FCSTD DOCUMENT  (FreeCAD 0.18.4R)
Label: Pino
License: All rights reserved
LicenseURL: http://en.wikipedia.org/wiki/All_rights_reserved
objects: Part::Part2DObjectPython×136, Part::Mirroring×9, App::DocumentObjectGroup×1
note: 145 computed .brp shape members not serialized (recipe doc carries the construction recipe); baked Part::Feature solids carry a one-line shape summary decoded from their .brp

FEATURE [Part::Part2DObjectPython] Line001  # Draft 2D object (typed FeaturePython)
  ChamferSize = 0
  Closed = false
  End = (5.7,0,0)
  FilletRadius = 0
  Length = 11.4
  MakeFace = true
  Points = (2) [(-5.7,0,0),(5.7,0,0)]
  Start = (-5.7,0,0)
  Subdivisions = 0
FEATURE [Part::Part2DObjectPython] Line003  # Draft 2D object (typed FeaturePython)
  ChamferSize = 0
  Closed = false
  End = (-5.7,0,0)
  FilletRadius = 0
  Length = 91.1954
  MakeFace = true
  Placement = pos=(-5.7,0,0) rot=(0,0,1;0rad)
  Points = (2) [(-88.088,23.6031,0),(-2.66454e-15,0,0)]
  Start = (-93.788,23.6031,0)
  Subdivisions = 0
FEATURE [Part::Part2DObjectPython] Line004  # Draft 2D object (typed FeaturePython)
  ChamferSize = 0
  Closed = true
  End = (89.7247,38.7673,0)
  FilletRadius = 0
  Length = 5.7
  MakeFace = false
  Placement = pos=(91.2,33.2615,0) rot=(0,0,1;0rad)
  Points = (2) [(0,0,0),(-1.47527,5.50578,0)]
  Start = (91.2,33.2615,0)
  Subdivisions = 0
FEATURE [Part::Part2DObjectPython] Line005  # Draft 2D object (typed FeaturePython)
  ChamferSize = 0
  Closed = false
  End = (-89.7247,38.7673,0)
  FilletRadius = 0
  Length = 5.7
  MakeFace = true
  Placement = pos=(-91.2,33.2615,0) rot=(0,0,1;0rad)
  Points = (2) [(0,0,0),(1.47527,5.50578,0)]
  Start = (-91.2,33.2615,0)
  Subdivisions = 0
FEATURE [Part::Part2DObjectPython] Line007  # Draft 2D object (typed FeaturePython)
  ChamferSize = 0
  Closed = false
  End = (-91.2,33.2615,0)
  FilletRadius = 0
  Length = 9.99914
  MakeFace = true
  Placement = pos=(-91.2,33.2615,0) rot=(0,0,1;0rad)
  Points = (2) [(-2.58797,-9.65843,0),(0,0,0)]
  Start = (-93.788,23.6031,0)
  Subdivisions = 0
FEATURE [Part::Part2DObjectPython] Line011  # Draft 2D object (typed FeaturePython)
  ChamferSize = 0
  Closed = true
  End = (78.3247,47.5148,0)
  FilletRadius = 0
  Length = 5.7
  MakeFace = false
  Placement = pos=(79.8,42.0091,0) rot=(0,0,1;0rad)
  Points = (2) [(0,0,0),(-1.47527,5.50578,0)]
  Start = (79.8,42.0091,0)
  Subdivisions = 0
FEATURE [Part::Part2DObjectPython] Line012  # Draft 2D object (typed FeaturePython)
  ChamferSize = 0
  Closed = false
  End = (-78.3247,47.5148,0)
  FilletRadius = 0
  Length = 5.7
  MakeFace = true
  Placement = pos=(-79.8,42.0091,0) rot=(0,0,1;0rad)
  Points = (2) [(0,0,0),(1.47527,5.50578,0)]
  Start = (-79.8,42.0091,0)
  Subdivisions = 0
FEATURE [Part::Part2DObjectPython] Line013  # Draft 2D object (typed FeaturePython)
  ChamferSize = 0
  Closed = false
  End = (81.2753,36.5033,0)
  FilletRadius = 0
  Length = 5.7
  MakeFace = true
  Placement = pos=(79.8,42.0091,0) rot=(0,0,1;0rad)
  Points = (2) [(0,0,0),(1.47527,-5.50578,0)]
  Start = (79.8,42.0091,0)
  Subdivisions = 0
FEATURE [Part::Part2DObjectPython] Line014  # Draft 2D object (typed FeaturePython)
  ChamferSize = 0
  Closed = false
  End = (-81.2753,36.5033,0)
  FilletRadius = 0
  Length = 5.7
  MakeFace = true
  Placement = pos=(-79.8,42.0091,0) rot=(0,0,1;0rad)
  Points = (2) [(0,0,0),(-1.47527,-5.50578,0)]
  Start = (-79.8,42.0091,0)
  Subdivisions = 0
FEATURE [Part::Part2DObjectPython] Line018  # Draft 2D object (typed FeaturePython)
  ChamferSize = 0
  Closed = true
  End = (66.9247,56.2624,0)
  FilletRadius = 0
  Length = 5.7
  MakeFace = false
  Placement = pos=(68.4,50.7566,0) rot=(0,0,1;0rad)
  Points = (2) [(0,0,0),(-1.47527,5.50578,0)]
  Start = (68.4,50.7566,0)
  Subdivisions = 0
FEATURE [Part::Part2DObjectPython] Line019  # Draft 2D object (typed FeaturePython)
  ChamferSize = 0
  Closed = false
  End = (-66.9247,56.2624,0)
  FilletRadius = 0
  Length = 5.7
  MakeFace = true
  Placement = pos=(-68.4,50.7566,0) rot=(0,0,1;0rad)
  Points = (2) [(0,0,0),(1.47527,5.50578,0)]
  Start = (-68.4,50.7566,0)
  Subdivisions = 0
FEATURE [Part::Part2DObjectPython] Line020  # Draft 2D object (typed FeaturePython)
  ChamferSize = 0
  Closed = false
  End = (69.8753,45.2508,0)
  FilletRadius = 0
  Length = 5.7
  MakeFace = true
  Placement = pos=(68.4,50.7566,0) rot=(0,0,1;0rad)
  Points = (2) [(0,0,0),(1.47527,-5.50578,0)]
  Start = (68.4,50.7566,0)
  Subdivisions = 0
FEATURE [Part::Part2DObjectPython] Line021  # Draft 2D object (typed FeaturePython)
  ChamferSize = 0
  Closed = false
  End = (-69.8753,45.2508,0)
  FilletRadius = 0
  Length = 5.7
  MakeFace = true
  Placement = pos=(-68.4,50.7566,0) rot=(0,0,1;0rad)
  Points = (2) [(0,0,0),(-1.47527,-5.50578,0)]
  Start = (-68.4,50.7566,0)
  Subdivisions = 0
FEATURE [Part::Part2DObjectPython] Line025  # Draft 2D object (typed FeaturePython)
  ChamferSize = 0
  Closed = true
  End = (55.5247,65.0099,0)
  FilletRadius = 0
  Length = 5.7
  MakeFace = false
  Placement = pos=(57,59.5041,0) rot=(0,0,1;0rad)
  Points = (2) [(0,0,0),(-1.47527,5.50578,0)]
  Start = (57,59.5041,0)
  Subdivisions = 0
FEATURE [Part::Part2DObjectPython] Line026  # Draft 2D object (typed FeaturePython)
  ChamferSize = 0
  Closed = false
  End = (-55.5247,65.0099,0)
  FilletRadius = 0
  Length = 5.7
  MakeFace = true
  Placement = pos=(-57,59.5041,0) rot=(0,0,1;0rad)
  Points = (2) [(0,0,0),(1.47527,5.50578,0)]
  Start = (-57,59.5041,0)
  Subdivisions = 0
FEATURE [Part::Part2DObjectPython] Line027  # Draft 2D object (typed FeaturePython)
  ChamferSize = 0
  Closed = false
  End = (58.4753,53.9983,0)
  FilletRadius = 0
  Length = 5.7
  MakeFace = true
  Placement = pos=(57,59.5041,0) rot=(0,0,1;0rad)
  Points = (2) [(0,0,0),(1.47527,-5.50578,0)]
  Start = (57,59.5041,0)
  Subdivisions = 0
FEATURE [Part::Part2DObjectPython] Line028  # Draft 2D object (typed FeaturePython)
  ChamferSize = 0
  Closed = false
  End = (-58.4753,53.9983,0)
  FilletRadius = 0
  Length = 5.7
  MakeFace = true
  Placement = pos=(-57,59.5041,0) rot=(0,0,1;0rad)
  Points = (2) [(0,0,0),(-1.47527,-5.50578,0)]
  Start = (-57,59.5041,0)
  Subdivisions = 0
FEATURE [Part::Part2DObjectPython] Line032  # Draft 2D object (typed FeaturePython)
  ChamferSize = 0
  Closed = true
  End = (44.1247,73.7574,0)
  FilletRadius = 0
  Length = 5.7
  MakeFace = false
  Placement = pos=(45.6,68.2516,0) rot=(0,0,1;0rad)
  Points = (2) [(0,0,0),(-1.47527,5.50578,0)]
  Start = (45.6,68.2516,0)
  Subdivisions = 0
FEATURE [Part::Part2DObjectPython] Line033  # Draft 2D object (typed FeaturePython)
  ChamferSize = 0
  Closed = false
  End = (-44.1247,73.7574,0)
  FilletRadius = 0
  Length = 5.7
  MakeFace = true
  Placement = pos=(-45.6,68.2516,0) rot=(0,0,1;0rad)
  Points = (2) [(0,0,0),(1.47527,5.50578,0)]
  Start = (-45.6,68.2516,0)
  Subdivisions = 0
FEATURE [Part::Part2DObjectPython] Line034  # Draft 2D object (typed FeaturePython)
  ChamferSize = 0
  Closed = false
  End = (47.0753,62.7459,0)
  FilletRadius = 0
  Length = 5.7
  MakeFace = true
  Placement = pos=(45.6,68.2516,0) rot=(0,0,1;0rad)
  Points = (2) [(0,0,0),(1.47527,-5.50578,0)]
  Start = (45.6,68.2516,0)
  Subdivisions = 0
FEATURE [Part::Part2DObjectPython] Line035  # Draft 2D object (typed FeaturePython)
  ChamferSize = 0
  Closed = false
  End = (-47.0753,62.7459,0)
  FilletRadius = 0
  Length = 5.7
  MakeFace = true
  Placement = pos=(-45.6,68.2516,0) rot=(0,0,1;0rad)
  Points = (2) [(0,0,0),(-1.47527,-5.50578,0)]
  Start = (-45.6,68.2516,0)
  Subdivisions = 0
FEATURE [Part::Part2DObjectPython] Line039  # Draft 2D object (typed FeaturePython)
  ChamferSize = 0
  Closed = true
  End = (32.7247,82.5049,0)
  FilletRadius = 0
  Length = 5.7
  MakeFace = false
  Placement = pos=(34.2,76.9992,0) rot=(0,0,1;0rad)
  Points = (2) [(0,0,0),(-1.47527,5.50578,0)]
  Start = (34.2,76.9992,0)
  Subdivisions = 0
FEATURE [Part::Part2DObjectPython] Line040  # Draft 2D object (typed FeaturePython)
  ChamferSize = 0
  Closed = false
  End = (-32.7247,82.5049,0)
  FilletRadius = 0
  Length = 5.7
  MakeFace = true
  Placement = pos=(-34.2,76.9992,0) rot=(0,0,1;0rad)
  Points = (2) [(0,0,0),(1.47527,5.50578,0)]
  Start = (-34.2,76.9992,0)
  Subdivisions = 0
FEATURE [Part::Part2DObjectPython] Line041  # Draft 2D object (typed FeaturePython)
  ChamferSize = 0
  Closed = false
  End = (35.6753,71.4934,0)
  FilletRadius = 0
  Length = 5.7
  MakeFace = true
  Placement = pos=(34.2,76.9992,0) rot=(0,0,1;0rad)
  Points = (2) [(0,0,0),(1.47527,-5.50578,0)]
  Start = (34.2,76.9992,0)
  Subdivisions = 0
FEATURE [Part::Part2DObjectPython] Line042  # Draft 2D object (typed FeaturePython)
  ChamferSize = 0
  Closed = false
  End = (-35.6753,71.4934,0)
  FilletRadius = 0
  Length = 5.7
  MakeFace = true
  Placement = pos=(-34.2,76.9992,0) rot=(0,0,1;0rad)
  Points = (2) [(0,0,0),(-1.47527,-5.50578,0)]
  Start = (-34.2,76.9992,0)
  Subdivisions = 0
FEATURE [Part::Part2DObjectPython] Line046  # Draft 2D object (typed FeaturePython)
  ChamferSize = 0
  Closed = true
  End = (21.3247,91.2525,0)
  FilletRadius = 0
  Length = 5.7
  MakeFace = false
  Placement = pos=(22.8,85.7467,0) rot=(0,0,1;0rad)
  Points = (2) [(0,0,0),(-1.47527,5.50578,0)]
  Start = (22.8,85.7467,0)
  Subdivisions = 0
FEATURE [Part::Part2DObjectPython] Line047  # Draft 2D object (typed FeaturePython)
  ChamferSize = 0
  Closed = false
  End = (-21.3247,91.2525,0)
  FilletRadius = 0
  Length = 5.7
  MakeFace = true
  Placement = pos=(-22.8,85.7467,0) rot=(0,0,1;0rad)
  Points = (2) [(0,0,0),(1.47527,5.50578,0)]
  Start = (-22.8,85.7467,0)
  Subdivisions = 0
FEATURE [Part::Part2DObjectPython] Line048  # Draft 2D object (typed FeaturePython)
  ChamferSize = 0
  Closed = false
  End = (24.2753,80.2409,0)
  FilletRadius = 0
  Length = 5.7
  MakeFace = true
  Placement = pos=(22.8,85.7467,0) rot=(0,0,1;0rad)
  Points = (2) [(0,0,0),(1.47527,-5.50578,0)]
  Start = (22.8,85.7467,0)
  Subdivisions = 0
FEATURE [Part::Part2DObjectPython] Line049  # Draft 2D object (typed FeaturePython)
  ChamferSize = 0
  Closed = false
  End = (-24.2753,80.2409,0)
  FilletRadius = 0
  Length = 5.7
  MakeFace = true
  Placement = pos=(-22.8,85.7467,0) rot=(0,0,1;0rad)
  Points = (2) [(0,0,0),(-1.47527,-5.50578,0)]
  Start = (-22.8,85.7467,0)
  Subdivisions = 0
FEATURE [Part::Part2DObjectPython] Line053  # Draft 2D object (typed FeaturePython)
  ChamferSize = 0
  Closed = true
  End = (9.92473,100,0)
  FilletRadius = 0
  Length = 5.7
  MakeFace = false
  Placement = pos=(11.4,94.4942,0) rot=(0,0,1;0rad)
  Points = (2) [(0,0,0),(-1.47527,5.50578,0)]
  Start = (11.4,94.4942,0)
  Subdivisions = 0
FEATURE [Part::Part2DObjectPython] Line054  # Draft 2D object (typed FeaturePython)
  ChamferSize = 0
  Closed = false
  End = (-9.92473,100,0)
  FilletRadius = 0
  Length = 5.7
  MakeFace = true
  Placement = pos=(-11.4,94.4942,0) rot=(0,0,1;0rad)
  Points = (2) [(0,0,0),(1.47527,5.50578,0)]
  Start = (-11.4,94.4942,0)
  Subdivisions = 0
FEATURE [Part::Part2DObjectPython] Line055  # Draft 2D object (typed FeaturePython)
  ChamferSize = 0
  Closed = false
  End = (12.8753,88.9884,0)
  FilletRadius = 0
  Length = 5.7
  MakeFace = true
  Placement = pos=(11.4,94.4942,0) rot=(0,0,1;0rad)
  Points = (2) [(0,0,0),(1.47527,-5.50578,0)]
  Start = (11.4,94.4942,0)
  Subdivisions = 0
FEATURE [Part::Part2DObjectPython] Line056  # Draft 2D object (typed FeaturePython)
  ChamferSize = 0
  Closed = false
  End = (-12.8753,88.9884,0)
  FilletRadius = 0
  Length = 5.7
  MakeFace = true
  Placement = pos=(-11.4,94.4942,0) rot=(0,0,1;0rad)
  Points = (2) [(0,0,0),(-1.47527,-5.50578,0)]
  Start = (-11.4,94.4942,0)
  Subdivisions = 0
FEATURE [Part::Part2DObjectPython] Line057  # Draft 2D object (typed FeaturePython)
  ChamferSize = 0
  Closed = false
  End = (-81.2753,36.5033,0)
  FilletRadius = 0
  Length = 8.74753
  MakeFace = true
  Placement = pos=(-89.7247,38.7673,0) rot=(0,0,1;0rad)
  Points = (2) [(0,0,0),(8.44946,-2.26403,0)]
  Start = (-89.7247,38.7673,0)
  Subdivisions = 0
FEATURE [Part::Part2DObjectPython] Line058  # Draft 2D object (typed FeaturePython)
  ChamferSize = 0
  Closed = false
  End = (-69.8753,45.2508,0)
  FilletRadius = 0
  Length = 8.74753
  MakeFace = true
  Placement = pos=(-78.3247,47.5148,0) rot=(0,0,1;0rad)
  Points = (2) [(0,0,0),(8.44946,-2.26403,0)]
  Start = (-78.3247,47.5148,0)
  Subdivisions = 0
FEATURE [Part::Part2DObjectPython] Line059  # Draft 2D object (typed FeaturePython)
  ChamferSize = 0
  Closed = false
  End = (-58.4753,53.9983,0)
  FilletRadius = 0
  Length = 8.74753
  MakeFace = true
  Placement = pos=(-66.9247,56.2624,0) rot=(0,0,1;0rad)
  Points = (2) [(0,0,0),(8.44946,-2.26403,0)]
  Start = (-66.9247,56.2624,0)
  Subdivisions = 0
FEATURE [Part::Part2DObjectPython] Line060  # Draft 2D object (typed FeaturePython)
  ChamferSize = 0
  Closed = false
  End = (-47.0753,62.7459,0)
  FilletRadius = 0
  Length = 8.74753
  MakeFace = true
  Placement = pos=(-55.5247,65.0099,0) rot=(0,0,1;0rad)
  Points = (2) [(0,0,0),(8.44946,-2.26403,0)]
  Start = (-55.5247,65.0099,0)
  Subdivisions = 0
FEATURE [Part::Part2DObjectPython] Line061  # Draft 2D object (typed FeaturePython)
  ChamferSize = 0
  Closed = false
  End = (-35.6753,71.4934,0)
  FilletRadius = 0
  Length = 8.74753
  MakeFace = true
  Placement = pos=(-44.1247,73.7574,0) rot=(0,0,1;0rad)
  Points = (2) [(0,0,0),(8.44946,-2.26403,0)]
  Start = (-44.1247,73.7574,0)
  Subdivisions = 0
FEATURE [Part::Part2DObjectPython] Line062  # Draft 2D object (typed FeaturePython)
  ChamferSize = 0
  Closed = false
  End = (-24.2753,80.2409,0)
  FilletRadius = 0
  Length = 8.74753
  MakeFace = true
  Placement = pos=(-32.7247,82.5049,0) rot=(0,0,1;0rad)
  Points = (2) [(0,0,0),(8.44946,-2.26403,0)]
  Start = (-32.7247,82.5049,0)
  Subdivisions = 0
FEATURE [Part::Part2DObjectPython] Line063  # Draft 2D object (typed FeaturePython)
  ChamferSize = 0
  Closed = false
  End = (-12.8753,88.9884,0)
  FilletRadius = 0
  Length = 8.74753
  MakeFace = true
  Placement = pos=(-21.3247,91.2525,0) rot=(0,0,1;0rad)
  Points = (2) [(0,0,0),(8.44946,-2.26403,0)]
  Start = (-21.3247,91.2525,0)
  Subdivisions = 0
FEATURE [Part::Mirroring] mirror  label="Mirror of Line003"
  Base = (0,91.4396,0)
  Normal = (-1,0,0)
  Source = -> Line003
FEATURE [Part::Mirroring] mirror001  label="Mirror of Line007"
  Base = (0,91.4396,0)
  Normal = (-1,0,0)
  Source = -> Line007
FEATURE [Part::Mirroring] mirror002  label="Mirror of Line057"
  Base = (0,91.4396,0)
  Normal = (-1,0,0)
  Source = -> Line057
FEATURE [Part::Mirroring] mirror003  label="Mirror of Line058"
  Base = (0,91.4396,0)
  Normal = (-1,0,0)
  Source = -> Line058
FEATURE [Part::Mirroring] mirror004  label="Mirror of Line059"
  Base = (0,91.4396,0)
  Normal = (-1,0,0)
  Source = -> Line059
FEATURE [Part::Mirroring] mirror005  label="Mirror of Line060"
  Base = (0,91.4396,0)
  Normal = (-1,0,0)
  Source = -> Line060
FEATURE [Part::Mirroring] mirror006  label="Mirror of Line061"
  Base = (0,91.4396,0)
  Normal = (-1,0,0)
  Source = -> Line061
FEATURE [Part::Mirroring] mirror007  label="Mirror of Line062"
  Base = (0,91.4396,0)
  Normal = (-1,0,0)
  Source = -> Line062
FEATURE [Part::Mirroring] mirror008  label="Mirror of Line063"
  Base = (0,91.4396,0)
  Normal = (-1,0,0)
  Source = -> Line063
FEATURE [Part::Part2DObjectPython] Line065  # Draft 2D object (typed FeaturePython)
  ChamferSize = 0
  Closed = false
  End = (9.92473,100,0)
  FilletRadius = 0
  Length = 19.8495
  MakeFace = true
  Placement = pos=(-9.92473,100,0) rot=(0,0,1;0rad)
  Points = (2) [(0,0,0),(19.8495,0,0)]
  Start = (-9.92473,100,0)
  Subdivisions = 0
FEATURE [App::DocumentObjectGroup] Group  label="Borders"
  Group = -> [Line003,Line007,Line005,Line057,Line014,Line012,Line058,Line021,Line019,Line028,Line026,Line059,Line060,Line035,Line033,Line061,Line042,Line040,Line062,Line049,Line047,Line063,Line056,Line054,Line065,Line053,Line055,mirror008,Line046,Line048,mirror007,Line039,Line041,mirror006,Line032,Line034,mirror005,Line025,Line027,mirror004,Line018,Line020,mirror003,Line011,Line013,mirror002,Line004,Line001,+2 more]
FEATURE [Part::Part2DObjectPython] Line  # Draft 2D object (typed FeaturePython)
  ChamferSize = 0
  Closed = false
  End = (0,8.82456,0)
  FilletRadius = 0
  Length = 8.82456
  MakeFace = true
  Points = (2) [(0,0,0),(0,8.82456,0)]
  Start = (0,0,0)
  Subdivisions = 0
FEATURE [Part::Part2DObjectPython] Line066  # Draft 2D object (typed FeaturePython)
  ChamferSize = 0
  Closed = false
  End = (5.7,0,0)
  FilletRadius = 0
  Length = 11.4
  MakeFace = true
  Points = (2) [(-5.7,0,0),(5.7,0,0)]
  Start = (-5.7,0,0)
  Subdivisions = 0
FEATURE [Part::Part2DObjectPython] Wire  # Draft 2D object (typed FeaturePython)
  ChamferSize = 0
  Closed = true
  End = (0.95,7.00161,0)
  FilletRadius = 0
  Length = 11.2
  MakeFace = false
  Placement = pos=(-0.95,7.00161,0) rot=(0,0,1;0rad)
  Points = (4) [(0,0,0),(0,3.7,0),(1.9,3.7,0),(1.9,0,0)]
  Start = (-0.95,7.00161,0)
  Subdivisions = 0
FEATURE [Part::Part2DObjectPython] Line067  # Draft 2D object (typed FeaturePython)
  ChamferSize = 0
  Closed = false
  End = (91.2,33.2615,0)
  FilletRadius = 0
  Length = 94.4172
  MakeFace = true
  Placement = pos=(0,8.82456,0) rot=(0,0,1;0rad)
  Points = (2) [(0,0,0),(91.2,24.437,0)]
  Start = (0,8.82456,0)
  Subdivisions = 0
FEATURE [Part::Part2DObjectPython] Line068  # Draft 2D object (typed FeaturePython)
  ChamferSize = 0
  Closed = false
  End = (-91.2,33.2615,0)
  FilletRadius = 0
  Length = 94.4172
  MakeFace = true
  Placement = pos=(0,8.82456,0) rot=(0,0,1;0rad)
  Points = (2) [(0,0,0),(-91.2,24.437,0)]
  Start = (0,8.82456,0)
  Subdivisions = 0
FEATURE [Part::Part2DObjectPython] Wire001  # Draft 2D object (typed FeaturePython)
  ChamferSize = 0
  Closed = true
  End = (84.1911,32.367,0)
  FilletRadius = 0
  Length = 11.2
  MakeFace = false
  Placement = pos=(80.6172,31.4094,0) rot=(0,0,1;0rad)
  Points = (4) [(0,0,0),(0.491756,-1.83526,0),(4.06568,-0.877629,0),(3.57393,0.95763,0)]
  Start = (80.6172,31.4094,0)
  Subdivisions = 0
FEATURE [Part::Part2DObjectPython] Wire002  # Draft 2D object (typed FeaturePython)
  ChamferSize = 0
  Closed = true
  End = (-84.1911,32.367,0)
  FilletRadius = 0
  Length = 11.2
  MakeFace = false
  Placement = pos=(-80.6172,31.4094,0) rot=(0,0,1;0rad)
  Points = (4) [(0,0,0),(-0.491756,-1.83526,0),(-4.06568,-0.877629,0),(-3.57393,0.95763,0)]
  Start = (-80.6172,31.4094,0)
  Subdivisions = 0
FEATURE [Part::Part2DObjectPython] Line069  # Draft 2D object (typed FeaturePython)
  ChamferSize = 0
  Closed = true
  End = (89.7247,38.7673,0)
  FilletRadius = 0
  Length = 5.7
  MakeFace = false
  Placement = pos=(91.2,33.2615,0) rot=(0,0,1;0rad)
  Points = (2) [(0,0,0),(-1.47527,5.50578,0)]
  Start = (91.2,33.2615,0)
  Subdivisions = 0
FEATURE [Part::Part2DObjectPython] Line070  # Draft 2D object (typed FeaturePython)
  ChamferSize = 0
  Closed = false
  End = (-89.7247,38.7673,0)
  FilletRadius = 0
  Length = 5.7
  MakeFace = true
  Placement = pos=(-91.2,33.2615,0) rot=(0,0,1;0rad)
  Points = (2) [(0,0,0),(1.47527,5.50578,0)]
  Start = (-91.2,33.2615,0)
  Subdivisions = 0
FEATURE [Part::Part2DObjectPython] Line071  # Draft 2D object (typed FeaturePython)
  ChamferSize = 0
  Closed = false
  End = (92.6753,27.7558,0)
  FilletRadius = 0
  Length = 5.7
  MakeFace = true
  Placement = pos=(91.2,33.2615,0) rot=(0,0,1;0rad)
  Points = (2) [(0,0,0),(1.47527,-5.50578,0)]
  Start = (91.2,33.2615,0)
  Subdivisions = 0
FEATURE [Part::Part2DObjectPython] Line072  # Draft 2D object (typed FeaturePython)
  ChamferSize = 0
  Closed = false
  End = (-92.6753,27.7558,0)
  FilletRadius = 0
  Length = 5.7
  MakeFace = true
  Placement = pos=(-91.2,33.2615,0) rot=(0,0,1;0rad)
  Points = (2) [(0,0,0),(-1.47527,-5.50578,0)]
  Start = (-91.2,33.2615,0)
  Subdivisions = 0
FEATURE [Part::Part2DObjectPython] Circle  # Draft 2D object (typed FeaturePython)
  FirstAngle = 0
  LastAngle = 0
  MakeFace = false
  Placement = pos=(47.0753,15.5373,0) rot=(0,0,1;0rad)
  Radius = 0.45
FEATURE [Part::Part2DObjectPython] Circle001  # Draft 2D object (typed FeaturePython)
  FirstAngle = 0
  LastAngle = 0
  MakeFace = false
  Placement = pos=(-47.0753,15.5373,0) rot=(0,0,1;0rad)
  Radius = 0.45
FEATURE [Part::Part2DObjectPython] Line073  # Draft 2D object (typed FeaturePython)
  ChamferSize = 0
  Closed = false
  End = (0,20.6267,0)
  FilletRadius = 0
  Length = 11.8021
  MakeFace = true
  Placement = pos=(0,8.82456,0) rot=(0,0,1;0rad)
  Points = (2) [(0,0,0),(0,11.8021,0)]
  Start = (0,8.82456,0)
  Subdivisions = 0
FEATURE [Part::Part2DObjectPython] Line074  # Draft 2D object (typed FeaturePython)
  ChamferSize = 0
  Closed = false
  End = (79.8,42.0091,0)
  FilletRadius = 0
  Length = 82.615
  MakeFace = true
  Placement = pos=(0,20.6267,0) rot=(0,0,1;0rad)
  Points = (2) [(0,0,0),(79.8,21.3823,0)]
  Start = (0,20.6267,0)
  Subdivisions = 0
FEATURE [Part::Part2DObjectPython] Line075  # Draft 2D object (typed FeaturePython)
  ChamferSize = 0
  Closed = false
  End = (-79.8,42.0091,0)
  FilletRadius = 0
  Length = 82.615
  MakeFace = true
  Placement = pos=(0,20.6267,0) rot=(0,0,1;0rad)
  Points = (2) [(0,0,0),(-79.8,21.3823,0)]
  Start = (0,20.6267,0)
  Subdivisions = 0
FEATURE [Part::Part2DObjectPython] Wire003  # Draft 2D object (typed FeaturePython)
  ChamferSize = 0
  Closed = true
  End = (72.7911,41.1145,0)
  FilletRadius = 0
  Length = 11.2
  MakeFace = false
  Placement = pos=(69.2172,40.1569,0) rot=(0,0,1;0rad)
  Points = (4) [(0,0,0),(0.491756,-1.83526,0),(4.06568,-0.877629,0),(3.57393,0.95763,0)]
  Start = (69.2172,40.1569,0)
  Subdivisions = 0
FEATURE [Part::Part2DObjectPython] Wire004  # Draft 2D object (typed FeaturePython)
  ChamferSize = 0
  Closed = true
  End = (-72.7911,41.1145,0)
  FilletRadius = 0
  Length = 11.2
  MakeFace = false
  Placement = pos=(-69.2172,40.1569,0) rot=(0,0,1;0rad)
  Points = (4) [(0,0,0),(-0.491756,-1.83526,0),(-4.06568,-0.877629,0),(-3.57393,0.95763,0)]
  Start = (-69.2172,40.1569,0)
  Subdivisions = 0
FEATURE [Part::Part2DObjectPython] Line076  # Draft 2D object (typed FeaturePython)
  ChamferSize = 0
  Closed = true
  End = (78.3247,47.5148,0)
  FilletRadius = 0
  Length = 5.7
  MakeFace = false
  Placement = pos=(79.8,42.0091,0) rot=(0,0,1;0rad)
  Points = (2) [(0,0,0),(-1.47527,5.50578,0)]
  Start = (79.8,42.0091,0)
  Subdivisions = 0
FEATURE [Part::Part2DObjectPython] Line077  # Draft 2D object (typed FeaturePython)
  ChamferSize = 0
  Closed = false
  End = (-78.3247,47.5148,0)
  FilletRadius = 0
  Length = 5.7
  MakeFace = true
  Placement = pos=(-79.8,42.0091,0) rot=(0,0,1;0rad)
  Points = (2) [(0,0,0),(1.47527,5.50578,0)]
  Start = (-79.8,42.0091,0)
  Subdivisions = 0
FEATURE [Part::Part2DObjectPython] Line078  # Draft 2D object (typed FeaturePython)
  ChamferSize = 0
  Closed = false
  End = (81.2753,36.5033,0)
  FilletRadius = 0
  Length = 5.7
  MakeFace = true
  Placement = pos=(79.8,42.0091,0) rot=(0,0,1;0rad)
  Points = (2) [(0,0,0),(1.47527,-5.50578,0)]
  Start = (79.8,42.0091,0)
  Subdivisions = 0
FEATURE [Part::Part2DObjectPython] Line079  # Draft 2D object (typed FeaturePython)
  ChamferSize = 0
  Closed = false
  End = (-81.2753,36.5033,0)
  FilletRadius = 0
  Length = 5.7
  MakeFace = true
  Placement = pos=(-79.8,42.0091,0) rot=(0,0,1;0rad)
  Points = (2) [(0,0,0),(-1.47527,-5.50578,0)]
  Start = (-79.8,42.0091,0)
  Subdivisions = 0
FEATURE [Part::Part2DObjectPython] Circle002  # Draft 2D object (typed FeaturePython)
  FirstAngle = 0
  LastAngle = 0
  MakeFace = false
  Placement = pos=(41.3753,25.8121,0) rot=(0,0,1;0rad)
  Radius = 0.45
FEATURE [Part::Part2DObjectPython] Circle003  # Draft 2D object (typed FeaturePython)
  FirstAngle = 0
  LastAngle = 0
  MakeFace = false
  Placement = pos=(-41.3753,25.8121,0) rot=(0,0,1;0rad)
  Radius = 0.45
FEATURE [Part::Part2DObjectPython] Line080  # Draft 2D object (typed FeaturePython)
  ChamferSize = 0
  Closed = false
  End = (0,32.4289,0)
  FilletRadius = 0
  Length = 11.8021
  MakeFace = true
  Placement = pos=(0,20.6267,0) rot=(0,0,1;0rad)
  Points = (2) [(0,0,0),(0,11.8021,0)]
  Start = (0,20.6267,0)
  Subdivisions = 0
FEATURE [Part::Part2DObjectPython] Line081  # Draft 2D object (typed FeaturePython)
  ChamferSize = 0
  Closed = false
  End = (68.4,50.7566,0)
  FilletRadius = 0
  Length = 70.8129
  MakeFace = true
  Placement = pos=(0,32.4289,0) rot=(0,0,1;0rad)
  Points = (2) [(0,0,0),(68.4,18.3277,0)]
  Start = (0,32.4289,0)
  Subdivisions = 0
FEATURE [Part::Part2DObjectPython] Line082  # Draft 2D object (typed FeaturePython)
  ChamferSize = 0
  Closed = false
  End = (-68.4,50.7566,0)
  FilletRadius = 0
  Length = 70.8129
  MakeFace = true
  Placement = pos=(0,32.4289,0) rot=(0,0,1;0rad)
  Points = (2) [(0,0,0),(-68.4,18.3277,0)]
  Start = (0,32.4289,0)
  Subdivisions = 0
FEATURE [Part::Part2DObjectPython] Wire005  # Draft 2D object (typed FeaturePython)
  ChamferSize = 0
  Closed = true
  End = (61.3911,49.8621,0)
  FilletRadius = 0
  Length = 11.2
  MakeFace = false
  Placement = pos=(57.8172,48.9044,0) rot=(0,0,1;0rad)
  Points = (4) [(0,0,0),(0.491756,-1.83526,0),(4.06568,-0.877629,0),(3.57393,0.95763,0)]
  Start = (57.8172,48.9044,0)
  Subdivisions = 0
FEATURE [Part::Part2DObjectPython] Wire006  # Draft 2D object (typed FeaturePython)
  ChamferSize = 0
  Closed = true
  End = (-61.3911,49.8621,0)
  FilletRadius = 0
  Length = 11.2
  MakeFace = false
  Placement = pos=(-57.8172,48.9044,0) rot=(0,0,1;0rad)
  Points = (4) [(0,0,0),(-0.491756,-1.83526,0),(-4.06568,-0.877629,0),(-3.57393,0.95763,0)]
  Start = (-57.8172,48.9044,0)
  Subdivisions = 0
FEATURE [Part::Part2DObjectPython] Line083  # Draft 2D object (typed FeaturePython)
  ChamferSize = 0
  Closed = true
  End = (66.9247,56.2624,0)
  FilletRadius = 0
  Length = 5.7
  MakeFace = false
  Placement = pos=(68.4,50.7566,0) rot=(0,0,1;0rad)
  Points = (2) [(0,0,0),(-1.47527,5.50578,0)]
  Start = (68.4,50.7566,0)
  Subdivisions = 0
FEATURE [Part::Part2DObjectPython] Line084  # Draft 2D object (typed FeaturePython)
  ChamferSize = 0
  Closed = false
  End = (-66.9247,56.2624,0)
  FilletRadius = 0
  Length = 5.7
  MakeFace = true
  Placement = pos=(-68.4,50.7566,0) rot=(0,0,1;0rad)
  Points = (2) [(0,0,0),(1.47527,5.50578,0)]
  Start = (-68.4,50.7566,0)
  Subdivisions = 0
FEATURE [Part::Part2DObjectPython] Line085  # Draft 2D object (typed FeaturePython)
  ChamferSize = 0
  Closed = false
  End = (69.8753,45.2508,0)
  FilletRadius = 0
  Length = 5.7
  MakeFace = true
  Placement = pos=(68.4,50.7566,0) rot=(0,0,1;0rad)
  Points = (2) [(0,0,0),(1.47527,-5.50578,0)]
  Start = (68.4,50.7566,0)
  Subdivisions = 0
FEATURE [Part::Part2DObjectPython] Line086  # Draft 2D object (typed FeaturePython)
  ChamferSize = 0
  Closed = false
  End = (-69.8753,45.2508,0)
  FilletRadius = 0
  Length = 5.7
  MakeFace = true
  Placement = pos=(-68.4,50.7566,0) rot=(0,0,1;0rad)
  Points = (2) [(0,0,0),(-1.47527,-5.50578,0)]
  Start = (-68.4,50.7566,0)
  Subdivisions = 0
FEATURE [Part::Part2DObjectPython] Circle004  # Draft 2D object (typed FeaturePython)
  FirstAngle = 0
  LastAngle = 0
  MakeFace = false
  Placement = pos=(35.6753,36.0869,0) rot=(0,0,1;0rad)
  Radius = 0.45
FEATURE [Part::Part2DObjectPython] Circle005  # Draft 2D object (typed FeaturePython)
  FirstAngle = 0
  LastAngle = 0
  MakeFace = false
  Placement = pos=(-35.6753,36.0869,0) rot=(0,0,1;0rad)
  Radius = 0.45
FEATURE [Part::Part2DObjectPython] Line087  # Draft 2D object (typed FeaturePython)
  ChamferSize = 0
  Closed = false
  End = (0,44.231,0)
  FilletRadius = 0
  Length = 11.8021
  MakeFace = true
  Placement = pos=(0,32.4289,0) rot=(0,0,1;0rad)
  Points = (2) [(0,0,0),(0,11.8021,0)]
  Start = (0,32.4289,0)
  Subdivisions = 0
FEATURE [Part::Part2DObjectPython] Line088  # Draft 2D object (typed FeaturePython)
  ChamferSize = 0
  Closed = false
  End = (57,59.5041,0)
  FilletRadius = 0
  Length = 59.0107
  MakeFace = true
  Placement = pos=(0,44.231,0) rot=(0,0,1;0rad)
  Points = (2) [(0,0,0),(57,15.2731,0)]
  Start = (0,44.231,0)
  Subdivisions = 0
FEATURE [Part::Part2DObjectPython] Line089  # Draft 2D object (typed FeaturePython)
  ChamferSize = 0
  Closed = false
  End = (-57,59.5041,0)
  FilletRadius = 0
  Length = 59.0107
  MakeFace = true
  Placement = pos=(0,44.231,0) rot=(0,0,1;0rad)
  Points = (2) [(0,0,0),(-57,15.2731,0)]
  Start = (0,44.231,0)
  Subdivisions = 0
FEATURE [Part::Part2DObjectPython] Wire007  # Draft 2D object (typed FeaturePython)
  ChamferSize = 0
  Closed = true
  End = (49.9911,58.6096,0)
  FilletRadius = 0
  Length = 11.2
  MakeFace = false
  Placement = pos=(46.4172,57.652,0) rot=(0,0,1;0rad)
  Points = (4) [(0,0,0),(0.491756,-1.83526,0),(4.06568,-0.877629,0),(3.57393,0.95763,0)]
  Start = (46.4172,57.652,0)
  Subdivisions = 0
FEATURE [Part::Part2DObjectPython] Wire008  # Draft 2D object (typed FeaturePython)
  ChamferSize = 0
  Closed = true
  End = (-49.9911,58.6096,0)
  FilletRadius = 0
  Length = 11.2
  MakeFace = false
  Placement = pos=(-46.4172,57.652,0) rot=(0,0,1;0rad)
  Points = (4) [(0,0,0),(-0.491756,-1.83526,0),(-4.06568,-0.877629,0),(-3.57393,0.95763,0)]
  Start = (-46.4172,57.652,0)
  Subdivisions = 0
FEATURE [Part::Part2DObjectPython] Line090  # Draft 2D object (typed FeaturePython)
  ChamferSize = 0
  Closed = true
  End = (55.5247,65.0099,0)
  FilletRadius = 0
  Length = 5.7
  MakeFace = false
  Placement = pos=(57,59.5041,0) rot=(0,0,1;0rad)
  Points = (2) [(0,0,0),(-1.47527,5.50578,0)]
  Start = (57,59.5041,0)
  Subdivisions = 0
FEATURE [Part::Part2DObjectPython] Line091  # Draft 2D object (typed FeaturePython)
  ChamferSize = 0
  Closed = false
  End = (-55.5247,65.0099,0)
  FilletRadius = 0
  Length = 5.7
  MakeFace = true
  Placement = pos=(-57,59.5041,0) rot=(0,0,1;0rad)
  Points = (2) [(0,0,0),(1.47527,5.50578,0)]
  Start = (-57,59.5041,0)
  Subdivisions = 0
FEATURE [Part::Part2DObjectPython] Line092  # Draft 2D object (typed FeaturePython)
  ChamferSize = 0
  Closed = false
  End = (58.4753,53.9983,0)
  FilletRadius = 0
  Length = 5.7
  MakeFace = true
  Placement = pos=(57,59.5041,0) rot=(0,0,1;0rad)
  Points = (2) [(0,0,0),(1.47527,-5.50578,0)]
  Start = (57,59.5041,0)
  Subdivisions = 0
FEATURE [Part::Part2DObjectPython] Line093  # Draft 2D object (typed FeaturePython)
  ChamferSize = 0
  Closed = false
  End = (-58.4753,53.9983,0)
  FilletRadius = 0
  Length = 5.7
  MakeFace = true
  Placement = pos=(-57,59.5041,0) rot=(0,0,1;0rad)
  Points = (2) [(0,0,0),(-1.47527,-5.50578,0)]
  Start = (-57,59.5041,0)
  Subdivisions = 0
FEATURE [Part::Part2DObjectPython] Circle006  # Draft 2D object (typed FeaturePython)
  FirstAngle = 0
  LastAngle = 0
  MakeFace = false
  Placement = pos=(29.9753,46.3618,0) rot=(0,0,1;0rad)
  Radius = 0.45
FEATURE [Part::Part2DObjectPython] Circle007  # Draft 2D object (typed FeaturePython)
  FirstAngle = 0
  LastAngle = 0
  MakeFace = false
  Placement = pos=(-29.9753,46.3618,0) rot=(0,0,1;0rad)
  Radius = 0.45
FEATURE [Part::Part2DObjectPython] Line094  # Draft 2D object (typed FeaturePython)
  ChamferSize = 0
  Closed = false
  End = (0,56.0332,0)
  FilletRadius = 0
  Length = 11.8021
  MakeFace = true
  Placement = pos=(0,44.231,0) rot=(0,0,1;0rad)
  Points = (2) [(0,0,0),(0,11.8021,0)]
  Start = (0,44.231,0)
  Subdivisions = 0
FEATURE [Part::Part2DObjectPython] Line095  # Draft 2D object (typed FeaturePython)
  ChamferSize = 0
  Closed = false
  End = (45.6,68.2516,0)
  FilletRadius = 0
  Length = 47.2086
  MakeFace = true
  Placement = pos=(0,56.0332,0) rot=(0,0,1;0rad)
  Points = (2) [(0,0,0),(45.6,12.2185,0)]
  Start = (0,56.0332,0)
  Subdivisions = 0
FEATURE [Part::Part2DObjectPython] Line096  # Draft 2D object (typed FeaturePython)
  ChamferSize = 0
  Closed = false
  End = (-45.6,68.2516,0)
  FilletRadius = 0
  Length = 47.2086
  MakeFace = true
  Placement = pos=(0,56.0332,0) rot=(0,0,1;0rad)
  Points = (2) [(0,0,0),(-45.6,12.2185,0)]
  Start = (0,56.0332,0)
  Subdivisions = 0
FEATURE [Part::Part2DObjectPython] Wire009  # Draft 2D object (typed FeaturePython)
  ChamferSize = 0
  Closed = true
  End = (38.5911,67.3571,0)
  FilletRadius = 0
  Length = 11.2
  MakeFace = false
  Placement = pos=(35.0172,66.3995,0) rot=(0,0,1;0rad)
  Points = (4) [(0,0,0),(0.491756,-1.83526,0),(4.06568,-0.877629,0),(3.57393,0.95763,0)]
  Start = (35.0172,66.3995,0)
  Subdivisions = 0
FEATURE [Part::Part2DObjectPython] Wire010  # Draft 2D object (typed FeaturePython)
  ChamferSize = 0
  Closed = true
  End = (-38.5911,67.3571,0)
  FilletRadius = 0
  Length = 11.2
  MakeFace = false
  Placement = pos=(-35.0172,66.3995,0) rot=(0,0,1;0rad)
  Points = (4) [(0,0,0),(-0.491756,-1.83526,0),(-4.06568,-0.877629,0),(-3.57393,0.95763,0)]
  Start = (-35.0172,66.3995,0)
  Subdivisions = 0
FEATURE [Part::Part2DObjectPython] Line097  # Draft 2D object (typed FeaturePython)
  ChamferSize = 0
  Closed = true
  End = (44.1247,73.7574,0)
  FilletRadius = 0
  Length = 5.7
  MakeFace = false
  Placement = pos=(45.6,68.2516,0) rot=(0,0,1;0rad)
  Points = (2) [(0,0,0),(-1.47527,5.50578,0)]
  Start = (45.6,68.2516,0)
  Subdivisions = 0
FEATURE [Part::Part2DObjectPython] Line098  # Draft 2D object (typed FeaturePython)
  ChamferSize = 0
  Closed = false
  End = (-44.1247,73.7574,0)
  FilletRadius = 0
  Length = 5.7
  MakeFace = true
  Placement = pos=(-45.6,68.2516,0) rot=(0,0,1;0rad)
  Points = (2) [(0,0,0),(1.47527,5.50578,0)]
  Start = (-45.6,68.2516,0)
  Subdivisions = 0
FEATURE [Part::Part2DObjectPython] Line099  # Draft 2D object (typed FeaturePython)
  ChamferSize = 0
  Closed = false
  End = (47.0753,62.7459,0)
  FilletRadius = 0
  Length = 5.7
  MakeFace = true
  Placement = pos=(45.6,68.2516,0) rot=(0,0,1;0rad)
  Points = (2) [(0,0,0),(1.47527,-5.50578,0)]
  Start = (45.6,68.2516,0)
  Subdivisions = 0
FEATURE [Part::Part2DObjectPython] Line100  # Draft 2D object (typed FeaturePython)
  ChamferSize = 0
  Closed = false
  End = (-47.0753,62.7459,0)
  FilletRadius = 0
  Length = 5.7
  MakeFace = true
  Placement = pos=(-45.6,68.2516,0) rot=(0,0,1;0rad)
  Points = (2) [(0,0,0),(-1.47527,-5.50578,0)]
  Start = (-45.6,68.2516,0)
  Subdivisions = 0
FEATURE [Part::Part2DObjectPython] Circle008  # Draft 2D object (typed FeaturePython)
  FirstAngle = 0
  LastAngle = 0
  MakeFace = false
  Placement = pos=(24.2753,56.6366,0) rot=(0,0,1;0rad)
  Radius = 0.45
FEATURE [Part::Part2DObjectPython] Circle009  # Draft 2D object (typed FeaturePython)
  FirstAngle = 0
  LastAngle = 0
  MakeFace = false
  Placement = pos=(-24.2753,56.6366,0) rot=(0,0,1;0rad)
  Radius = 0.45
FEATURE [Part::Part2DObjectPython] Line101  # Draft 2D object (typed FeaturePython)
  ChamferSize = 0
  Closed = false
  End = (0,67.8353,0)
  FilletRadius = 0
  Length = 11.8021
  MakeFace = true
  Placement = pos=(0,56.0332,0) rot=(0,0,1;0rad)
  Points = (2) [(0,0,0),(0,11.8021,0)]
  Start = (0,56.0332,0)
  Subdivisions = 0
FEATURE [Part::Part2DObjectPython] Line102  # Draft 2D object (typed FeaturePython)
  ChamferSize = 0
  Closed = false
  End = (34.2,76.9992,0)
  FilletRadius = 0
  Length = 35.4064
  MakeFace = true
  Placement = pos=(0,67.8353,0) rot=(0,0,1;0rad)
  Points = (2) [(0,0,0),(34.2,9.16386,0)]
  Start = (0,67.8353,0)
  Subdivisions = 0
FEATURE [Part::Part2DObjectPython] Line103  # Draft 2D object (typed FeaturePython)
  ChamferSize = 0
  Closed = false
  End = (-34.2,76.9992,0)
  FilletRadius = 0
  Length = 35.4064
  MakeFace = true
  Placement = pos=(0,67.8353,0) rot=(0,0,1;0rad)
  Points = (2) [(0,0,0),(-34.2,9.16386,0)]
  Start = (0,67.8353,0)
  Subdivisions = 0
FEATURE [Part::Part2DObjectPython] Wire011  # Draft 2D object (typed FeaturePython)
  ChamferSize = 0
  Closed = true
  End = (27.1911,76.1046,0)
  FilletRadius = 0
  Length = 11.2
  MakeFace = false
  Placement = pos=(23.6172,75.147,0) rot=(0,0,1;0rad)
  Points = (4) [(0,0,0),(0.491756,-1.83526,0),(4.06568,-0.877629,0),(3.57393,0.95763,0)]
  Start = (23.6172,75.147,0)
  Subdivisions = 0
FEATURE [Part::Part2DObjectPython] Wire012  # Draft 2D object (typed FeaturePython)
  ChamferSize = 0
  Closed = true
  End = (-27.1911,76.1046,0)
  FilletRadius = 0
  Length = 11.2
  MakeFace = false
  Placement = pos=(-23.6172,75.147,0) rot=(0,0,1;0rad)
  Points = (4) [(0,0,0),(-0.491756,-1.83526,0),(-4.06568,-0.877629,0),(-3.57393,0.95763,0)]
  Start = (-23.6172,75.147,0)
  Subdivisions = 0
FEATURE [Part::Part2DObjectPython] Line104  # Draft 2D object (typed FeaturePython)
  ChamferSize = 0
  Closed = true
  End = (32.7247,82.5049,0)
  FilletRadius = 0
  Length = 5.7
  MakeFace = false
  Placement = pos=(34.2,76.9992,0) rot=(0,0,1;0rad)
  Points = (2) [(0,0,0),(-1.47527,5.50578,0)]
  Start = (34.2,76.9992,0)
  Subdivisions = 0
FEATURE [Part::Part2DObjectPython] Line105  # Draft 2D object (typed FeaturePython)
  ChamferSize = 0
  Closed = false
  End = (-32.7247,82.5049,0)
  FilletRadius = 0
  Length = 5.7
  MakeFace = true
  Placement = pos=(-34.2,76.9992,0) rot=(0,0,1;0rad)
  Points = (2) [(0,0,0),(1.47527,5.50578,0)]
  Start = (-34.2,76.9992,0)
  Subdivisions = 0
FEATURE [Part::Part2DObjectPython] Line106  # Draft 2D object (typed FeaturePython)
  ChamferSize = 0
  Closed = false
  End = (35.6753,71.4934,0)
  FilletRadius = 0
  Length = 5.7
  MakeFace = true
  Placement = pos=(34.2,76.9992,0) rot=(0,0,1;0rad)
  Points = (2) [(0,0,0),(1.47527,-5.50578,0)]
  Start = (34.2,76.9992,0)
  Subdivisions = 0
FEATURE [Part::Part2DObjectPython] Line107  # Draft 2D object (typed FeaturePython)
  ChamferSize = 0
  Closed = false
  End = (-35.6753,71.4934,0)
  FilletRadius = 0
  Length = 5.7
  MakeFace = true
  Placement = pos=(-34.2,76.9992,0) rot=(0,0,1;0rad)
  Points = (2) [(0,0,0),(-1.47527,-5.50578,0)]
  Start = (-34.2,76.9992,0)
  Subdivisions = 0
FEATURE [Part::Part2DObjectPython] Circle010  # Draft 2D object (typed FeaturePython)
  FirstAngle = 0
  LastAngle = 0
  MakeFace = false
  Placement = pos=(18.5753,66.9115,0) rot=(0,0,1;0rad)
  Radius = 0.45
FEATURE [Part::Part2DObjectPython] Circle011  # Draft 2D object (typed FeaturePython)
  FirstAngle = 0
  LastAngle = 0
  MakeFace = false
  Placement = pos=(-18.5753,66.9115,0) rot=(0,0,1;0rad)
  Radius = 0.45
FEATURE [Part::Part2DObjectPython] Line108  # Draft 2D object (typed FeaturePython)
  ChamferSize = 0
  Closed = false
  End = (0,79.6375,0)
  FilletRadius = 0
  Length = 11.8021
  MakeFace = true
  Placement = pos=(0,67.8353,0) rot=(0,0,1;0rad)
  Points = (2) [(0,0,0),(0,11.8021,0)]
  Start = (0,67.8353,0)
  Subdivisions = 0
FEATURE [Part::Part2DObjectPython] Line109  # Draft 2D object (typed FeaturePython)
  ChamferSize = 0
  Closed = false
  End = (22.8,85.7467,0)
  FilletRadius = 0
  Length = 23.6043
  MakeFace = true
  Placement = pos=(0,79.6375,0) rot=(0,0,1;0rad)
  Points = (2) [(0,0,0),(22.8,6.10924,0)]
  Start = (0,79.6375,0)
  Subdivisions = 0
FEATURE [Part::Part2DObjectPython] Line110  # Draft 2D object (typed FeaturePython)
  ChamferSize = 0
  Closed = false
  End = (-22.8,85.7467,0)
  FilletRadius = 0
  Length = 23.6043
  MakeFace = true
  Placement = pos=(0,79.6375,0) rot=(0,0,1;0rad)
  Points = (2) [(0,0,0),(-22.8,6.10924,0)]
  Start = (0,79.6375,0)
  Subdivisions = 0
FEATURE [Part::Part2DObjectPython] Wire013  # Draft 2D object (typed FeaturePython)
  ChamferSize = 0
  Closed = true
  End = (15.7911,84.8522,0)
  FilletRadius = 0
  Length = 11.2
  MakeFace = false
  Placement = pos=(12.2172,83.8945,0) rot=(0,0,1;0rad)
  Points = (4) [(0,0,0),(0.491756,-1.83526,0),(4.06568,-0.877629,0),(3.57393,0.95763,0)]
  Start = (12.2172,83.8945,0)
  Subdivisions = 0
FEATURE [Part::Part2DObjectPython] Wire014  # Draft 2D object (typed FeaturePython)
  ChamferSize = 0
  Closed = true
  End = (-15.7911,84.8522,0)
  FilletRadius = 0
  Length = 11.2
  MakeFace = false
  Placement = pos=(-12.2172,83.8945,0) rot=(0,0,1;0rad)
  Points = (4) [(0,0,0),(-0.491756,-1.83526,0),(-4.06568,-0.877629,0),(-3.57393,0.95763,0)]
  Start = (-12.2172,83.8945,0)
  Subdivisions = 0
FEATURE [Part::Part2DObjectPython] Line111  # Draft 2D object (typed FeaturePython)
  ChamferSize = 0
  Closed = true
  End = (21.3247,91.2525,0)
  FilletRadius = 0
  Length = 5.7
  MakeFace = false
  Placement = pos=(22.8,85.7467,0) rot=(0,0,1;0rad)
  Points = (2) [(0,0,0),(-1.47527,5.50578,0)]
  Start = (22.8,85.7467,0)
  Subdivisions = 0
FEATURE [Part::Part2DObjectPython] Line112  # Draft 2D object (typed FeaturePython)
  ChamferSize = 0
  Closed = false
  End = (-21.3247,91.2525,0)
  FilletRadius = 0
  Length = 5.7
  MakeFace = true
  Placement = pos=(-22.8,85.7467,0) rot=(0,0,1;0rad)
  Points = (2) [(0,0,0),(1.47527,5.50578,0)]
  Start = (-22.8,85.7467,0)
  Subdivisions = 0
FEATURE [Part::Part2DObjectPython] Line113  # Draft 2D object (typed FeaturePython)
  ChamferSize = 0
  Closed = false
  End = (24.2753,80.2409,0)
  FilletRadius = 0
  Length = 5.7
  MakeFace = true
  Placement = pos=(22.8,85.7467,0) rot=(0,0,1;0rad)
  Points = (2) [(0,0,0),(1.47527,-5.50578,0)]
  Start = (22.8,85.7467,0)
  Subdivisions = 0
FEATURE [Part::Part2DObjectPython] Line114  # Draft 2D object (typed FeaturePython)
  ChamferSize = 0
  Closed = false
  End = (-24.2753,80.2409,0)
  FilletRadius = 0
  Length = 5.7
  MakeFace = true
  Placement = pos=(-22.8,85.7467,0) rot=(0,0,1;0rad)
  Points = (2) [(0,0,0),(-1.47527,-5.50578,0)]
  Start = (-22.8,85.7467,0)
  Subdivisions = 0
FEATURE [Part::Part2DObjectPython] Circle012  # Draft 2D object (typed FeaturePython)
  FirstAngle = 0
  LastAngle = 0
  MakeFace = false
  Placement = pos=(12.8753,77.1863,0) rot=(0,0,1;0rad)
  Radius = 0.45
FEATURE [Part::Part2DObjectPython] Circle013  # Draft 2D object (typed FeaturePython)
  FirstAngle = 0
  LastAngle = 0
  MakeFace = false
  Placement = pos=(-12.8753,77.1863,0) rot=(0,0,1;0rad)
  Radius = 0.45
FEATURE [Part::Part2DObjectPython] Line115  # Draft 2D object (typed FeaturePython)
  ChamferSize = 0
  Closed = false
  End = (0,91.4396,0)
  FilletRadius = 0
  Length = 11.8021
  MakeFace = true
  Placement = pos=(0,79.6375,0) rot=(0,0,1;0rad)
  Points = (2) [(0,0,0),(0,11.8021,0)]
  Start = (0,79.6375,0)
  Subdivisions = 0
FEATURE [Part::Part2DObjectPython] Line116  # Draft 2D object (typed FeaturePython)
  ChamferSize = 0
  Closed = false
  End = (11.4,94.4942,0)
  FilletRadius = 0
  Length = 11.8021
  MakeFace = true
  Placement = pos=(0,91.4396,0) rot=(0,0,1;0rad)
  Points = (2) [(0,0,0),(11.4,3.05462,0)]
  Start = (0,91.4396,0)
  Subdivisions = 0
FEATURE [Part::Part2DObjectPython] Line117  # Draft 2D object (typed FeaturePython)
  ChamferSize = 0
  Closed = false
  End = (-11.4,94.4942,0)
  FilletRadius = 0
  Length = 11.8021
  MakeFace = true
  Placement = pos=(0,91.4396,0) rot=(0,0,1;0rad)
  Points = (2) [(0,0,0),(-11.4,3.05462,0)]
  Start = (0,91.4396,0)
  Subdivisions = 0
FEATURE [Part::Part2DObjectPython] Wire015  # Draft 2D object (typed FeaturePython)
  ChamferSize = 0
  Closed = true
  End = (4.39108,93.5997,0)
  FilletRadius = 0
  Length = 11.2
  MakeFace = false
  Placement = pos=(0.817159,92.6421,0) rot=(0,0,1;0rad)
  Points = (4) [(0,0,0),(0.491756,-1.83526,0),(4.06568,-0.877629,0),(3.57393,0.95763,0)]
  Start = (0.817159,92.6421,0)
  Subdivisions = 0
FEATURE [Part::Part2DObjectPython] Wire016  # Draft 2D object (typed FeaturePython)
  ChamferSize = 0
  Closed = true
  End = (-4.39108,93.5997,0)
  FilletRadius = 0
  Length = 11.2
  MakeFace = false
  Placement = pos=(-0.817159,92.6421,0) rot=(0,0,1;0rad)
  Points = (4) [(0,0,0),(-0.491756,-1.83526,0),(-4.06568,-0.877629,0),(-3.57393,0.95763,0)]
  Start = (-0.817159,92.6421,0)
  Subdivisions = 0
FEATURE [Part::Part2DObjectPython] Line118  # Draft 2D object (typed FeaturePython)
  ChamferSize = 0
  Closed = true
  End = (9.92473,100,0)
  FilletRadius = 0
  Length = 5.7
  MakeFace = false
  Placement = pos=(11.4,94.4942,0) rot=(0,0,1;0rad)
  Points = (2) [(0,0,0),(-1.47527,5.50578,0)]
  Start = (11.4,94.4942,0)
  Subdivisions = 0
FEATURE [Part::Part2DObjectPython] Line119  # Draft 2D object (typed FeaturePython)
  ChamferSize = 0
  Closed = false
  End = (-9.92473,100,0)
  FilletRadius = 0
  Length = 5.7
  MakeFace = true
  Placement = pos=(-11.4,94.4942,0) rot=(0,0,1;0rad)
  Points = (2) [(0,0,0),(1.47527,5.50578,0)]
  Start = (-11.4,94.4942,0)
  Subdivisions = 0
FEATURE [Part::Part2DObjectPython] Line120  # Draft 2D object (typed FeaturePython)
  ChamferSize = 0
  Closed = false
  End = (12.8753,88.9884,0)
  FilletRadius = 0
  Length = 5.7
  MakeFace = true
  Placement = pos=(11.4,94.4942,0) rot=(0,0,1;0rad)
  Points = (2) [(0,0,0),(1.47527,-5.50578,0)]
  Start = (11.4,94.4942,0)
  Subdivisions = 0
FEATURE [Part::Part2DObjectPython] Line121  # Draft 2D object (typed FeaturePython)
  ChamferSize = 0
  Closed = false
  End = (-12.8753,88.9884,0)
  FilletRadius = 0
  Length = 5.7
  MakeFace = true
  Placement = pos=(-11.4,94.4942,0) rot=(0,0,1;0rad)
  Points = (2) [(0,0,0),(-1.47527,-5.50578,0)]
  Start = (-11.4,94.4942,0)
  Subdivisions = 0
FEATURE [Part::Part2DObjectPython] Circle014  # Draft 2D object (typed FeaturePython)
  FirstAngle = 0
  LastAngle = 0
  MakeFace = false
  Placement = pos=(7.17527,87.4611,0) rot=(0,0,1;0rad)
  Radius = 0.45
FEATURE [Part::Part2DObjectPython] Circle015  # Draft 2D object (typed FeaturePython)
  FirstAngle = 0
  LastAngle = 0
  MakeFace = false
  Placement = pos=(-7.17527,87.4611,0) rot=(0,0,1;0rad)
  Radius = 0.45
FEATURE [Part::Part2DObjectPython] Circle016  # Draft 2D object (typed FeaturePython)
  FirstAngle = 0
  LastAngle = 0
  MakeFace = false
  Placement = pos=(0,95.7198,0) rot=(0,0,1;0rad)
  Radius = 0.45
FEATURE [Part::Part2DObjectPython] Circle017  # Draft 2D object (typed FeaturePython)
  FirstAngle = 0
  LastAngle = 0
  MakeFace = false
  Placement = pos=(19.95,20.0712,0) rot=(0,0,1;0rad)
  Radius = 1.6
FEATURE [Part::Part2DObjectPython] Circle018  # Draft 2D object (typed FeaturePython)
  FirstAngle = 0
  LastAngle = 0
  MakeFace = false
  Placement = pos=(-19.95,20.0712,0) rot=(0,0,1;0rad)
  Radius = 1.6
FEATURE [Part::Part2DObjectPython] Circle019  # Draft 2D object (typed FeaturePython)
  FirstAngle = 0
  LastAngle = 0
  MakeFace = false
  Placement = pos=(8.55,64.2252,0) rot=(0,0,1;0rad)
  Radius = 1.6
FEATURE [Part::Part2DObjectPython] Circle020  # Draft 2D object (typed FeaturePython)
  FirstAngle = 0
  LastAngle = 0
  MakeFace = false
  Placement = pos=(-8.55,64.2252,0) rot=(0,0,1;0rad)
  Radius = 1.6
